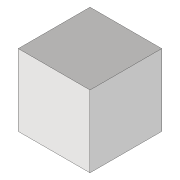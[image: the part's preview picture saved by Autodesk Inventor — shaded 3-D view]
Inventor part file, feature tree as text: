
AUTODESK INVENTOR PART (.ipt)
format: ipt  version: 2020 (Build 240168000, 168)  size: 77,824 bytes
history: native  units: mm
features: extrude x1, sketch x1
ambient origin geometry x8: Origin, YZ Plane, XZ Plane, XY Plane, X Axis, Y Axis, Z Axis, Center Point
bodies: Volumenkörper1 (feature_tree)
feature tree (2):
  extrude  "Extrusion1"  Depth=1.0mm
  sketch  "Skizze1"  dims[d0=1.0mm d1=1.0mm d2=1.0mm d3=0.0mm]
